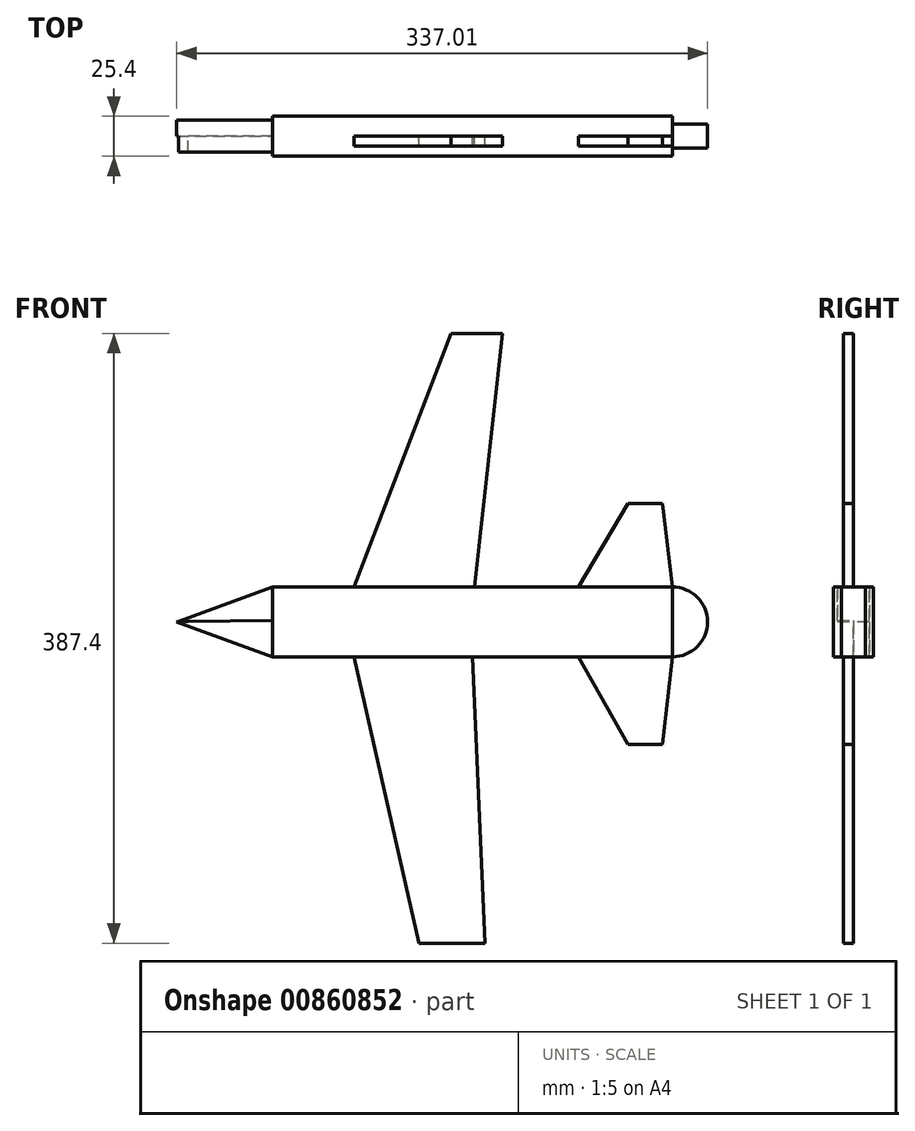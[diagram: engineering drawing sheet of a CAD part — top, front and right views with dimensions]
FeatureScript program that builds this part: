
annotation { "Feature Type Name" : "Feature", "Feature Type Description" : "" }
export const myFeature = defineFeature(function(context is Context, id is Id, definition is map)
    precondition{}
    {
        {
            var Q0;
            Q0=qCreatedBy(makeId("Front.planeOp"),FACE);
            var sketch = newSketch(context, id + "F0", { "sketchPlane" : qUnion([Q0])});
            skLineSegment(sketch, "E0.bottom", {"start": v(-127.8, -39.33) * mm, "end": v(126.2, -39.33) * mm});
            skLineSegment(sketch, "E0.top", {"start": v(-127.8, 5.12) * mm, "end": v(126.2, 5.12) * mm});
            skLineSegment(sketch, "E0.left", {"start": v(-127.8, -39.33) * mm, "end": v(-127.8, 5.12) * mm});
            skLineSegment(sketch, "E0.right", {"start": v(126.2, -39.33) * mm, "end": v(126.2, 5.12) * mm});
            skLineSegment(sketch, "E1", {"start": v(-127.8, 5.12) * mm, "end": v(-188.65, -17.1) * mm});
            skPoint(sketch, "E1.endSnap0", {"position": v(-127.8, -17.1) * mm});
            skLineSegment(sketch, "E2", {"start": v(-188.65, -17.1) * mm, "end": v(-127.8, -39.33) * mm});
            skCircle(sketch, "E3", {"center": v(126.2, -17.1) * mm, "radius": 22.17 * mm});
            skLineSegment(sketch, "E4", {"start": v(66.33, 5.12) * mm, "end": v(98, 58.07) * mm});
            skLineSegment(sketch, "E5", {"start": v(98, 58.07) * mm, "end": v(119.81, 58.07) * mm});
            skLineSegment(sketch, "E6", {"start": v(119.81, 58.07) * mm, "end": v(126.2, 5.12) * mm});
            skLineSegment(sketch, "E7", {"start": v(66.33, -39.33) * mm, "end": v(98, -94.82) * mm});
            skLineSegment(sketch, "E8", {"start": v(98, -94.82) * mm, "end": v(119.81, -94.82) * mm});
            skLineSegment(sketch, "E9", {"start": v(119.81, -94.82) * mm, "end": v(126.2, -39.33) * mm});
            skLineSegment(sketch, "E10", {"start": v(-76.26, 5.12) * mm, "end": v(-14.65, 166.2) * mm});
            skLineSegment(sketch, "E11", {"start": v(-14.65, 166.2) * mm, "end": v(18.23, 166.2) * mm});
            skLineSegment(sketch, "E12", {"start": v(18.23, 166.2) * mm, "end": v(0, 0) * mm});
            skLineSegment(sketch, "E13", {"start": v(-76.26, -39.33) * mm, "end": v(-34.9, -221.2) * mm});
            skLineSegment(sketch, "E14", {"start": v(-34.9, -221.2) * mm, "end": v(7.15, -221.2) * mm});
            skLineSegment(sketch, "E15", {"start": v(7.15, -221.2) * mm, "end": v(-0.8, -39.33) * mm});
            skSolve(sketch);
        }
        {
            var Q0;
            {var subQ0=sQuery(id+"F0.wireOp",EDGE,"E10");Q0=makeQuery(id+"F0.imprint","IMPRINT",FACE,{"disambiguationData":[TD([[makeQuery(id+"F0.imprint","IMPRINT",EDGE,{"derivedFrom":subQ0}),-1.0]])]});}
            extrude(context, id + "F1", {"entities" : qUnion([Q0]), "depth" : 6.35 * mm, "offsetDistance" : 25.4 * mm});
        }
        {
            var Q0;
            {var subQ0=sQuery(id+"F0.wireOp",EDGE,"E13");Q0=makeQuery(id+"F0.imprint","IMPRINT",FACE,{"disambiguationData":[TD([[makeQuery(id+"F0.imprint","IMPRINT",EDGE,{"derivedFrom":subQ0}),1.0]])]});}
            extrude(context, id + "F2", {"entities" : qUnion([Q0]), "depth" : 6.35 * mm, "offsetDistance" : 25.4 * mm});
        }
        {
            var Q0;
            {var subQ5=sQuery(id+"F0.wireOp",EDGE,"E0.left");Q0=makeQuery(id+"F0.imprint","IMPRINT",FACE,{"disambiguationData":[TD([[makeQuery(id+"F0.imprint","IMPRINT",EDGE,{"derivedFrom":subQ5}),-1.0]])]});}
            extrude(context, id + "F3", {"entities" : qUnion([Q0]), "depth" : 12.7 * mm, "offsetDistance" : 25.4 * mm});
        }
        {
            var Q0;
            {var subQ5=sQuery(id+"F0.wireOp",EDGE,"E0.left");Q0=makeQuery(id+"F0.imprint","IMPRINT",FACE,{"disambiguationData":[TD([[makeQuery(id+"F0.imprint","IMPRINT",EDGE,{"derivedFrom":subQ5}),-1.0]])]});}
            extrude(context, id + "F4", {"entities" : qUnion([Q0]), "operationType" : NewBodyOperationType.ADD, "oppositeDirection" : true, "depth" : 12.7 * mm, "offsetDistance" : 25.4 * mm});
        }
        {
            var Q0;
            {var subQ2=sQuery(id+"F0.wireOp",EDGE,"E7");Q0=makeQuery(id+"F0.imprint","IMPRINT",FACE,{"disambiguationData":[TD([[makeQuery(id+"F0.imprint","IMPRINT",EDGE,{"derivedFrom":subQ2}),1.0]])]});}
            extrude(context, id + "F5", {"entities" : qUnion([Q0]), "operationType" : NewBodyOperationType.ADD, "depth" : 6.35 * mm, "offsetDistance" : 25.4 * mm});
        }
        {
            var Q0;
            {var subQ2=sQuery(id+"F0.wireOp",EDGE,"E4");Q0=makeQuery(id+"F0.imprint","IMPRINT",FACE,{"disambiguationData":[TD([[makeQuery(id+"F0.imprint","IMPRINT",EDGE,{"derivedFrom":subQ2}),-1.0]])]});}
            extrude(context, id + "F6", {"entities" : qUnion([Q0]), "operationType" : NewBodyOperationType.ADD, "depth" : 6.35 * mm, "offsetDistance" : 25.4 * mm});
        }
        {
            var Q0;
            {var subQ0=sQuery(id+"F0.wireOp",EDGE,"E3");var subQ1=sQuery(id+"F0.wireOp",EDGE,"E0.right");var subQ2=makeQuery(id+"F0.imprint","INTERSECT",VERTEX,{"disambiguationData":[OD(0.0)],"derivedFrom":[subQ1,subQ0]});Q0=makeQuery(id+"F0.imprint","IMPRINT",FACE,{"disambiguationData":[TD([[makeQuery(id+"F0.imprint","IMPRINT",EDGE,{"disambiguationData":[TD([[subQ2,-1.0]])],"derivedFrom":subQ1}),1.0]])]});}
            extrude(context, id + "F7", {"entities" : qUnion([Q0]), "operationType" : NewBodyOperationType.ADD, "depth" : 12.7 * mm, "offsetDistance" : 25.4 * mm});
        }
        {
            var Q0;
            {var subQ0=sQuery(id+"F0.wireOp",EDGE,"E3");var subQ1=sQuery(id+"F0.wireOp",EDGE,"E0.right");var subQ2=makeQuery(id+"F0.imprint","INTERSECT",VERTEX,{"disambiguationData":[OD(0.0)],"derivedFrom":[subQ1,subQ0]});Q0=makeQuery(id+"F0.imprint","IMPRINT",FACE,{"disambiguationData":[TD([[makeQuery(id+"F0.imprint","IMPRINT",EDGE,{"disambiguationData":[TD([[subQ2,-1.0]])],"derivedFrom":subQ1}),1.0]])]});}
            extrude(context, id + "F8", {"entities" : qUnion([Q0]), "operationType" : NewBodyOperationType.ADD, "oppositeDirection" : true, "depth" : 12.7 * mm, "offsetDistance" : 25.4 * mm});
        }
        {
            var Q0;
            {var subQ0=sQuery(id+"F0.wireOp",EDGE,"E3");var subQ1=sQuery(id+"F0.wireOp",EDGE,"E0.right");var subQ2=makeQuery(id+"F0.imprint","INTERSECT",VERTEX,{"disambiguationData":[OD(0.0)],"derivedFrom":[subQ1,subQ0]});Q0=makeQuery(id+"F0.imprint","IMPRINT",FACE,{"disambiguationData":[TD([[makeQuery(id+"F0.imprint","IMPRINT",EDGE,{"disambiguationData":[TD([[subQ2,-1.0]])],"derivedFrom":subQ1}),-1.0]])]});}
            extrude(context, id + "F9", {"entities" : qUnion([Q0]), "operationType" : NewBodyOperationType.ADD, "depth" : 7.62 * mm, "offsetDistance" : 25.4 * mm});
        }
        {
            var Q0;
            {var subQ0=sQuery(id+"F0.wireOp",EDGE,"E3");var subQ1=sQuery(id+"F0.wireOp",EDGE,"E0.right");var subQ2=makeQuery(id+"F0.imprint","INTERSECT",VERTEX,{"disambiguationData":[OD(0.0)],"derivedFrom":[subQ1,subQ0]});Q0=makeQuery(id+"F0.imprint","IMPRINT",FACE,{"disambiguationData":[TD([[makeQuery(id+"F0.imprint","IMPRINT",EDGE,{"disambiguationData":[TD([[subQ2,-1.0]])],"derivedFrom":subQ1}),-1.0]])]});}
            extrude(context, id + "F10", {"entities" : qUnion([Q0]), "operationType" : NewBodyOperationType.ADD, "oppositeDirection" : true, "depth" : 7.62 * mm, "offsetDistance" : 25.4 * mm});
        }
        {
            var Q0;
            Q0=makeQuery(id+"F0.imprint","IMPRINT",FACE,{"disambiguationData":[TD([[makeQuery(id+"F0.imprint","IMPRINT",EDGE,{"derivedFrom":sQuery(id+"F0.wireOp",EDGE,"E0.left")}),1.0]])]});
            var sketch = newSketch(context, id + "F11", { "sketchPlane" : qUnion([Q0])});
            skLineSegment(sketch, "E16", {"start": v(-188.27, -16.73) * mm, "end": v(-123.22, -16.73) * mm});
            skLineSegment(sketch, "E17", {"start": v(-98.96, -15.73) * mm, "end": v(-181.62, -16.73) * mm});
            skSolve(sketch);
        }
        {
            var Q0;
            Q0 = qSketchRegion(id + "F11", true);
            var Q1;
            {var subQ0=sQuery(id+"F11.wireOp",EDGE,"E17");var subQ1=sQuery(id+"F11.wireOp",EDGE,"E16");var subQ2=makeQuery(id+"F11.imprint","INTERSECT",VERTEX,{"derivedFrom":[subQ1,subQ0]});Q1=makeQuery(id+"F11.imprint","IMPRINT",FACE,{"disambiguationData":[TD([[makeQuery(id+"F11.imprint","IMPRINT",EDGE,{"disambiguationData":[TD([[subQ2,1.0]])],"derivedFrom":subQ1}),1.0]])]});}
            extrude(context, id + "F12", {"entities" : qUnion([Q0, Q1]), "operationType" : NewBodyOperationType.ADD, "depth" : 10.16 * mm, "offsetDistance" : 25.4 * mm});
        }
        {
            var Q0;
            Q0=makeQuery(id+"F0.imprint","IMPRINT",FACE,{"disambiguationData":[TD([[makeQuery(id+"F0.imprint","IMPRINT",EDGE,{"derivedFrom":sQuery(id+"F0.wireOp",EDGE,"E0.left")}),1.0]])]});
            extrude(context, id + "F13", {"entities" : qUnion([Q0]), "operationType" : NewBodyOperationType.ADD, "oppositeDirection" : true, "depth" : 10.16 * mm, "offsetDistance" : 25.4 * mm});
        }
    });
